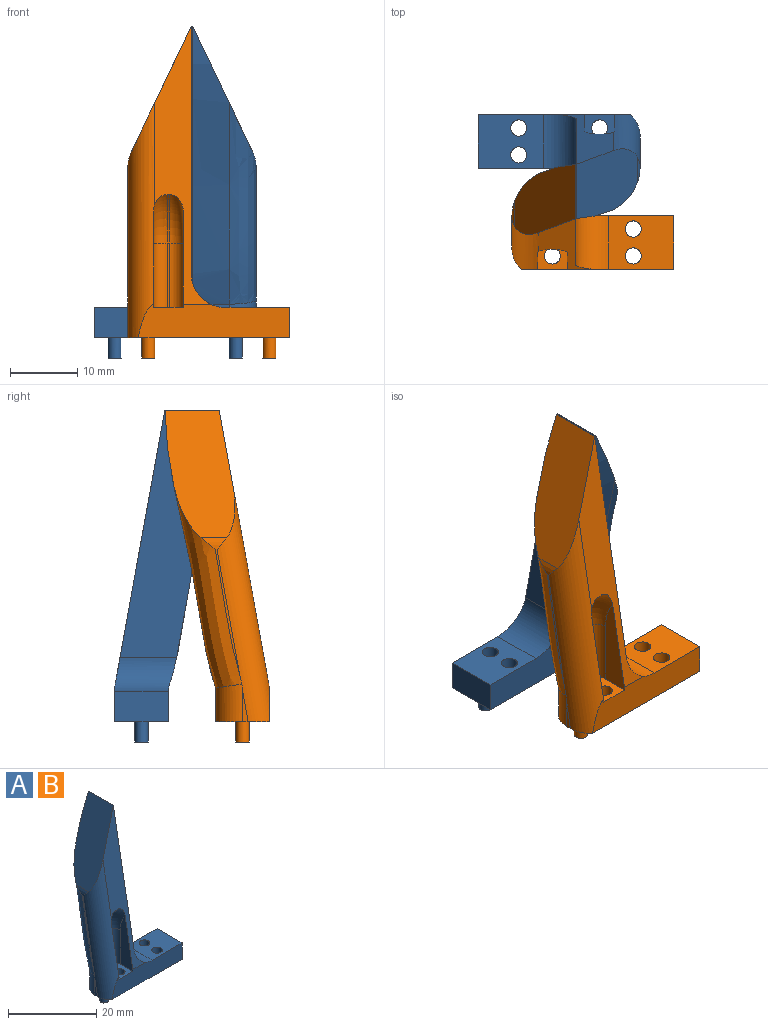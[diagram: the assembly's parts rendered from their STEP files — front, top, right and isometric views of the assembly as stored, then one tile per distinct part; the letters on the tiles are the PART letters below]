
ASSEMBLY  parts=2 mates=1
PART A: 32 faces, bbox 24.8x17.2x50.3 mm
  f0: plane 18.63x3.63mm, normal (-1,0,0), area 5.3mm2, adj f28,f29,f30
  f1: plane 22.51x5mm, normal (0,-1,0), area 100.9mm2, adj f2,f8,f9,f16,f17,f18,f19,f28
  f2: plane 42.08x9.01mm, normal (0,-0.98,0.18), area 131.4mm2, adj f1,f5,f7,f9,f13,f14,f15,f28
  f3: extruded ~41.29x8.22mm, area 202.1mm2, adj f4,f5,f7,f29,f31
  f4: plane 20x5mm, normal (0,1,0), area 94.5mm2, adj f3,f17,f18,f19,f27,f31
  f5: plane 37.24x14.69mm, normal (1,0,0), area 313.7mm2, adj f2,f3,f7,f31
  f6: plane 4.64x0.84mm, normal (-1,0,0), area 1.9mm2, adj f19,f27,f28
  f7: plane 19.44x10.83mm, normal (-0.9,0,0.43), area 169.7mm2, adj f2,f3,f5,f28,f29,f30
  f8: plane 14.24x4mm, normal (1,0,0), area 37.6mm2, adj f1,f12,f13,f16,f28
  f9: plane 14.25x4mm, normal (-1,0,0), area 37.6mm2, adj f1,f2,f11,f15,f16
  f10: plane 9.56x0.4mm, normal (0,-1,0), area 3.8mm2, adj f11,f12,f14,f16
  f11: cylinder r=2mm len=9.56mm, axis (0,0,-1), area 30mm2, adj f9,f10,f15,f16
  f12: cylinder r=2mm len=9.56mm, axis (0,0,1), area 30mm2, adj f8,f10,f13,f16
  f13: torus R=8mm, axis (-1,0,0), area 21.5mm2, adj f2,f8,f12,f14,f28
  f14: cylinder r=10mm len=7.2mm, axis (-1,0,0), area 3.2mm2, adj f2,f10,f13,f15
  f15: torus R=8mm, axis (-1,0,0), area 20.9mm2, adj f2,f9,f11,f14
  f16: plane 6x4.4mm, normal (0,0,1), area 20.2mm2, adj f1,f8,f9,f10,f11,f12,f22
  f17: plane 8x4.5mm, normal (1,0,0), area 36mm2, adj f1,f4,f18,f19
  f18: plane 9.6x8mm, normal (0,0,1), area 67.8mm2, adj f1,f4,f17,f20,f21,f31
  f19: plane 24.06x8.06mm, normal (0,0,-1), area 167.6mm2, adj f1,f4,f6,f17,f20,f21,f22,f23
  f20: cylinder r=1.2mm len=4.5mm, axis (0,0,-1), area 33.9mm2, adj f18,f19
  f21: cylinder r=1.2mm len=4.5mm, axis (0,0,-1), area 33.9mm2, adj f18,f19
  f22: cylinder r=1.2mm len=4.5mm, axis (0,0,-1), area 33.9mm2, adj f16,f19
  f23: cylinder r=0.97mm len=3mm, axis (0,0,1), area 18.4mm2, adj f19,f24
  f24: plane 1.95x1.95mm, normal (0,0,-1), area 3mm2, adj f23
  f25: cylinder r=0.97mm len=3mm, axis (0,0,1), area 18.4mm2, adj f19,f26
  f26: plane 1.95x1.95mm, normal (0,0,-1), area 3mm2, adj f25
  f27: cylinder r=4mm len=5.6mm, axis (0,0,-1), area 33.3mm2, adj f4,f6,f19,f28,f29
  f28: cylinder r=4mm len=35.47mm, axis (0,0.18,0.98), area 175.9mm2, adj f0,f1,f2,f6,f7,f8,f13,f19
  f29: bspline ~35.14x11.04mm, area 157.3mm2, adj f0,f3,f7,f27,f28,f30
  f30: cylinder r=4mm len=3.8mm, axis (0,1,0), area 3.6mm2, adj f0,f7,f28,f29
  f31: cylinder r=5mm len=9.22mm, axis (0,-1,0), area 64mm2, adj f1,f2,f3,f4,f5,f18
PART B: same geometry as A
PLACE A rot(axis=(0,0,1),180deg) t=(9.89,23.05,30.03)mm
PLACE B t=(14.88,8.05,30.03)mm
MATE slider B.f17 <-> A.f17  axis (1,0,0) through (26.88,12.05,32.28)mm
